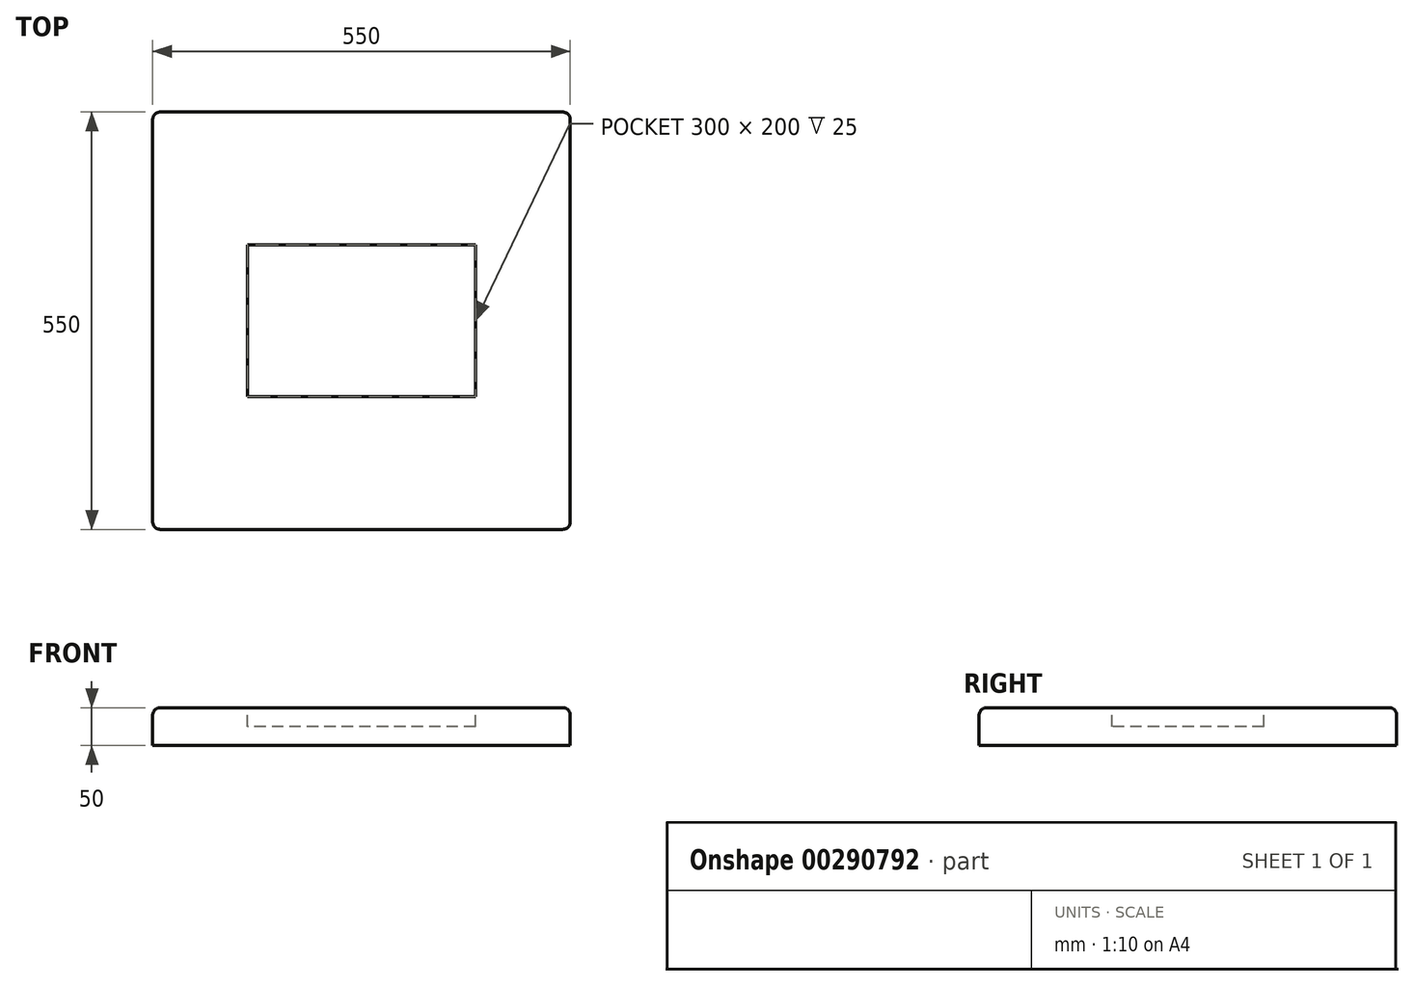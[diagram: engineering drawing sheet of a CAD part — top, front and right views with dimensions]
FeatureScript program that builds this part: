
annotation { "Feature Type Name" : "Feature", "Feature Type Description" : "" }
export const myFeature = defineFeature(function(context is Context, id is Id, definition is map)
    precondition{}
    {
        {
            var Q0;
            Q0=qCreatedBy(makeId("Top.planeOp"),FACE);
            var sketch = newSketch(context, id + "F0", { "sketchPlane" : qUnion([Q0])});
            skLineSegment(sketch, "E0.bottom", {"start": v(275, 275) * mm, "end": v(-275, 275) * mm});
            skLineSegment(sketch, "E0.top", {"start": v(275, -275) * mm, "end": v(-275, -275) * mm});
            skLineSegment(sketch, "E0.left", {"start": v(275, 275) * mm, "end": v(275, -275) * mm});
            skLineSegment(sketch, "E0.right", {"start": v(-275, 275) * mm, "end": v(-275, -275) * mm});
            skPoint(sketch, "E0.middle", {"position": v(0, 0) * mm});
            skSolve(sketch);
        }
        {
            var Q0;
            Q0=makeQuery(id+"F0.imprint","IMPRINT",FACE,{"disambiguationData":[TD([[makeQuery(id+"F0.imprint","IMPRINT",EDGE,{"derivedFrom":sQuery(id+"F0.wireOp",EDGE,"E0.bottom")}),1.0]])]});
            extrude(context, id + "F1", {"entities" : qUnion([Q0]), "depth" : 50 * mm});
        }
        {
            var Q0;
            Q0=makeQuery(id+"F1.opExtrude","CAP_EDGE",EDGE,{"disambiguationData":[OSD([sQuery(id+"F0.wireOp",EDGE,"E0.top")])],"isStart":false});
            var Q1;
            Q1=makeQuery(id+"F1.opExtrude","CAP_FACE",FACE,{"disambiguationData":[OSD([sQuery(id+"F0.wireOp",EDGE,"E0.bottom"),sQuery(id+"F0.wireOp",EDGE,"E0.top"),sQuery(id+"F0.wireOp",EDGE,"E0.left"),sQuery(id+"F0.wireOp",EDGE,"E0.right")])],"isStart":false});
            var Q2;
            Q2=makeQuery(id+"F1.opExtrude","CAP_EDGE",EDGE,{"disambiguationData":[OSD([sQuery(id+"F0.wireOp",EDGE,"E0.bottom")])],"isStart":false});
            var Q3;
            Q3=makeQuery(id+"F1.opExtrude","CAP_EDGE",EDGE,{"disambiguationData":[OSD([sQuery(id+"F0.wireOp",EDGE,"E0.left")])],"isStart":false});
            fillet(context, id + "F2", {"entities" : qUnion([Q0, Q1, Q2, Q3]), "radius" : 10 * mm, "tangentPropagation" : true, "allowEdgeOverflow" : false});
        }
        {
            var Q0;
            Q0=makeQuery(id+"F1.opExtrude","SWEPT_EDGE",EDGE,{"disambiguationData":[OSD([sQuery(id+"F0.wireOp",EDGE,"E0.top"),sQuery(id+"F0.wireOp",EDGE,"E0.left")])]});
            var Q1;
            Q1=makeQuery(id+"F1.opExtrude","SWEPT_EDGE",EDGE,{"disambiguationData":[OSD([sQuery(id+"F0.wireOp",EDGE,"E0.top"),sQuery(id+"F0.wireOp",EDGE,"E0.right")])]});
            var Q2;
            Q2=makeQuery(id+"F1.opExtrude","SWEPT_EDGE",EDGE,{"disambiguationData":[OSD([sQuery(id+"F0.wireOp",EDGE,"E0.bottom"),sQuery(id+"F0.wireOp",EDGE,"E0.left")])]});
            var Q3;
            Q3=makeQuery(id+"F1.opExtrude","SWEPT_EDGE",EDGE,{"disambiguationData":[OSD([sQuery(id+"F0.wireOp",EDGE,"E0.bottom"),sQuery(id+"F0.wireOp",EDGE,"E0.right")])]});
            fillet(context, id + "F3", {"entities" : qUnion([Q0, Q1, Q2, Q3]), "radius" : 10 * mm, "tangentPropagation" : true, "allowEdgeOverflow" : false});
        }
        {
            var Q0;
            Q0=makeQuery(id+"F1.opExtrude","CAP_FACE",FACE,{"disambiguationData":[OSD([sQuery(id+"F0.wireOp",EDGE,"E0.bottom"),sQuery(id+"F0.wireOp",EDGE,"E0.top"),sQuery(id+"F0.wireOp",EDGE,"E0.left"),sQuery(id+"F0.wireOp",EDGE,"E0.right")])],"isStart":false});
            var sketch = newSketch(context, id + "F4", { "sketchPlane" : qUnion([Q0])});
            skLineSegment(sketch, "E1.bottom", {"start": v(150, 100) * mm, "end": v(-150, 100) * mm});
            skLineSegment(sketch, "E1.top", {"start": v(150, -100) * mm, "end": v(-150, -100) * mm});
            skLineSegment(sketch, "E1.left", {"start": v(150, 100) * mm, "end": v(150, -100) * mm});
            skLineSegment(sketch, "E1.right", {"start": v(-150, 100) * mm, "end": v(-150, -100) * mm});
            skPoint(sketch, "E1.middle", {"position": v(0, 0) * mm});
            skSolve(sketch);
        }
        {
            var Q0;
            Q0=makeQuery(id+"F4.imprint","IMPRINT",FACE,{"disambiguationData":[TD([[makeQuery(id+"F4.imprint","IMPRINT",EDGE,{"derivedFrom":sQuery(id+"F4.wireOp",EDGE,"E1.bottom")}),1.0]])]});
            extrude(context, id + "F5", {"entities" : qUnion([Q0]), "operationType" : NewBodyOperationType.REMOVE, "oppositeDirection" : true, "depth" : 25 * mm});
        }
    });
